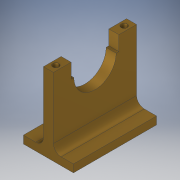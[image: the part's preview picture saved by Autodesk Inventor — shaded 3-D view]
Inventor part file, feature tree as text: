
AUTODESK INVENTOR PART (.ipt)
format: ipt  version: 2019 (Build 230136000, 136)  size: 146,944 bytes
history: native  units: mm
features: extrude x3, sketch x3, fillet x1
ambient origin geometry x8: Origin, YZ Plane, XZ Plane, XY Plane, X Axis, Y Axis, Z Axis, Center Point
bodies: Solid1 (feature_tree)
feature tree (7):
  extrude  "Extrusion1"  Depth=3250.0mm
  extrude  "Extrusion2"  Depth=500.0mm
  fillet  "Fillet1"  Radius=325.0mm
  extrude  "Extrusion3"  Depth=1100.0mm
  sketch  "Sketch1"  dims[d8=650.0mm d9=0.0mm d10=3250.0mm]
  sketch  "Sketch2"  dims[d11=500.0mm d12=0.0mm d13=500.0mm d14=325.0mm]
  sketch  "Sketch3"  dims[d15=481.017mm d16=400.0mm d17=325.0mm d18=481.017mm d19=400.0mm d20=1100.0mm d21=0.0mm]
